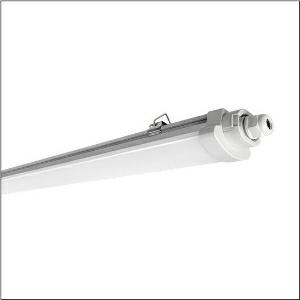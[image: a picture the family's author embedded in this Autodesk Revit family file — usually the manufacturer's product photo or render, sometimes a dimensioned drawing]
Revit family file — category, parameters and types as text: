
# Revit family: monsun_r__41_51fk20mk440a003_a901
name_source: partatom
category: Lighting Fixtures
units: mm (PartAtom-declared; Revit-internal decimal feet)

## family parameters
Cut with Voids When Loaded = No
Host = Face
Light Source = No
Part Type = Normal
Room Calculation Point = No
Round Connector Dimension = Use Diameter
Shared = No

## types (1)
- --- (1 x LED, 4000 lm, 30 W, 4000K)
    Apparent Load = 30 VA
    CIE Flux Codes = 44 74 92 92 100
    Color Rendering = 80
    Color Temperature = 4000K
    Default Elevation = 1800 mm
    Description = Monsun® 41, damp-proof luminaire, primary optical cover: diffuser, of PC, frosted, light emission: direct distribution, primary light characteristic: symmetric, installation type: surface-mounted, suspended mounting, LED, rated luminous flux: 4.000lm, luminous efficacy: 130lm/W, light colour: 840, colour temperature: 4000K, control gear: ON/OFF Multilumen, with terminal, 3-pole, through-wiring: 3x 1.5mm², mains connection: 220..240V, AC, 50/60Hz, rated input power: 30W, housing, luminaire housing, of PC, grey, length: 1.200mm, width: 79mm, height: 52mm, end cap, of PC, grey, ceiling mounting element, of stainless steel (V2A), protection rating (complete): IP65, insulation class (complete): insulation class II (safety insulation), certification: CE, UKCA, protection symbol: D, impact resistance: IK08, permissible operating ambient temperature: -20..+35°C, corresponds to IFS (International Featured Standards) requirements for safety and quality in the food industry, contact your sales advisor before using the luminaires in applications with unclear chemical exposure, large temperature fluctuations or condensation-forming humidity, packaging unit: 1 piece
    Height = 54 mm
    Lamp = 1 x LED
    Lamp Light Flux = 4000 lm
    Lamp Power = 30 W
    Lamp count = 1
    Length = 1200 mm
    Luminous efficacy = 133 lm/W
    Manufacturer = Siteco
    ModVariant = No
    Model = 51FK20MK440A003
    Mounting Place = Ceiling
    Mounting Type = Surface mounted
    Number of Poles = 1
    OnlyDefault = Yes
    Power Factor = 1
    Product Name = Monsun® 41
    Product group = damp-proof luminaire
    ProductGroupID = 301
    Protection Class = Protection class II
    Protection Degree = IP 65
    RLX_Detail_Level = 1
    RLX_Emergency_Light_Flux = 0 lm
    RLX_Emergency_Type = 0
    RLX_Emergency_Type_DB = No
    RlxData = <blob elided: 31865 chars, md5=2a01ab9f>
    Socket = socket
    Standby Power = 0 W
    System Light Flux = 4000 lm
    System Power = 30 W
    Type Comments = factory setting: luminous flux: 100 % | (HIGH)
    Type Image = l_1007037.jpg
    URL = http://relux.com
    VarID = @adj_196171
    Voltage = 0 V
    Weight = 0.00 kg
    Width = 79 mm

## geometry (parser evidence)
native form markers: Blend x4, Sweep x13
no freeform markers — native parametric forms only
